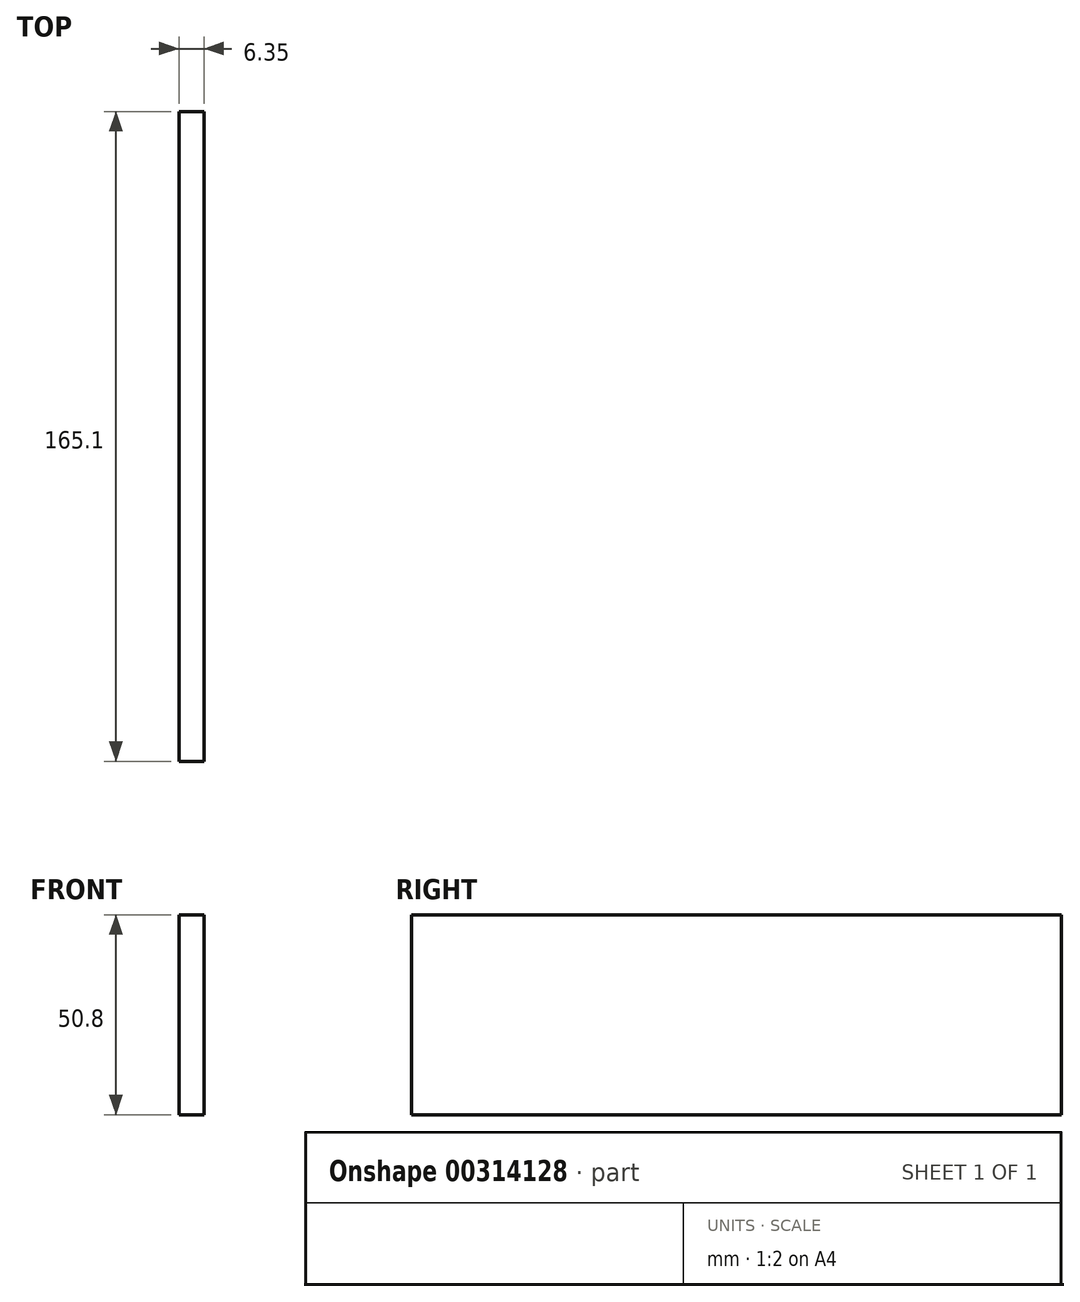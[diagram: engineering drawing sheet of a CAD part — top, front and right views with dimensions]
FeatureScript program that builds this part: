
annotation { "Feature Type Name" : "Feature", "Feature Type Description" : "" }
export const myFeature = defineFeature(function(context is Context, id is Id, definition is map)
    precondition{}
    {
        {
            var Q0;
            Q0=qCreatedBy(makeId("Right.planeOp"),FACE);
            var sketch = newSketch(context, id + "F0", { "sketchPlane" : qUnion([Q0])});
            skLineSegment(sketch, "E0.bottom", {"start": v(0, 0) * mm, "end": v(165.1, 0) * mm});
            skLineSegment(sketch, "E0.top", {"start": v(0, 50.8) * mm, "end": v(165.1, 50.8) * mm});
            skLineSegment(sketch, "E0.left", {"start": v(0, 0) * mm, "end": v(0, 50.8) * mm});
            skLineSegment(sketch, "E0.right", {"start": v(165.1, 0) * mm, "end": v(165.1, 50.8) * mm});
            skSolve(sketch);
        }
        {
            var Q0;
            Q0=makeQuery(id+"F0.imprint","IMPRINT",FACE,{"disambiguationData":[TD([[makeQuery(id+"F0.imprint","IMPRINT",EDGE,{"derivedFrom":sQuery(id+"F0.wireOp",EDGE,"E0.bottom")}),1.0]])]});
            extrude(context, id + "F1", {"entities" : qUnion([Q0]), "depth" : 6.35 * mm});
        }
    });
